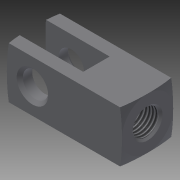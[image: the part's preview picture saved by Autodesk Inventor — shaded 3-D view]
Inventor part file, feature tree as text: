
AUTODESK INVENTOR PART (.ipt)
format: ipt  version: 2014 (Build 180170000, 170)  size: 210,432 bytes
history: native  units: in
note: dims shown in document units (in); Inventor stores cm internally (conversion verified against a paired STEP export)
features: other x126, sketch x7, revolve x3, extrude x2, hole x2
ambient origin geometry x8: Origin, YZ Plane, XZ Plane, XY Plane, X Axis, Y Axis, Z Axis, Center Point
bodies: Solid1 (feature_tree)
feature tree (140):
  extrude  "Extrusion1"  Depth=0.75in TaperAngle=0.0deg
  extrude  "Extrusion2"  TaperAngle=360.0deg  [1 undecoded]
  hole  "Hole1"  [1 undecoded]
  hole  "Hole2"  [1 undecoded]
  revolve  "Revolution1"  [1 undecoded]
  revolve  "Revolution2"  [1 undecoded]
  revolve  "Revolution3"  [1 undecoded]
  other  "dummy_XY"
  other  "dummy_YZ"
  other  "dummy_ZX"
  other  "dummy_X"
  other  "dummy_Y"
  other  "dummy_Z"
  other  "dummy_Center"
  other  "h1_XY"
  other  "h1_YZ"
  other  "h1_ZX"
  other  "h1_X"
  other  "h1_Y"
  other  "h1_Z"
  other  "h1_Center"
  other  "h2_XY"
  other  "h2_YZ"
  other  "h2_ZX"
  other  "h2_X"
  other  "h2_Y"
  other  "h2_Z"
  other  "h2_Center"
  other  "l1_XY"
  other  "l1_YZ"
  other  "l1_ZX"
  other  "l1_X"
  other  "l1_Y"
  other  "l1_Z"
  other  "l1_Center"
  other  "l11_XY"
  other  "l11_YZ"
  other  "l11_ZX"
  other  "l11_X"
  other  "l11_Y"
  other  "l11_Z"
  other  "l11_Center"
  other  "l12_XY"
  other  "l12_YZ"
  other  "l12_ZX"
  other  "l12_X"
  other  "l12_Y"
  other  "l12_Z"
  other  "l12_Center"
  other  "l2_XY"
  other  "l2_YZ"
  other  "l2_ZX"
  other  "l2_X"
  other  "l2_Y"
  other  "l2_Z"
  other  "l2_Center"
  other  "l21_XY"
  other  "l21_YZ"
  other  "l21_ZX"
  other  "l21_X"
  other  "l21_Y"
  other  "l21_Z"
  other  "l21_Center"
  other  "l22_XY"
  other  "l22_YZ"
  other  "l22_ZX"
  other  "l22_X"
  other  "l22_Y"
  other  "l22_Z"
  other  "l22_Center"
  other  "piston_rod_clevis_XY"
  other  "piston_rod_clevis_YZ"
  other  "piston_rod_clevis_ZX"
  other  "piston_rod_clevis_X"
  other  "piston_rod_clevis_Y"
  other  "piston_rod_clevis_Z"
  other  "piston_rod_clevis_Center"
  other  "rod_clevis_body_XY"
  other  "rod_clevis_body_YZ"
  other  "rod_clevis_body_ZX"
  other  "rod_clevis_body_X"
  other  "rod_clevis_body_Y"
  other  "rod_clevis_body_Z"
  other  "rod_clevis_body_Center"
  other  "th1_XY"
  other  "th1_YZ"
  other  "th1_ZX"
  other  "th1_X"
  other  "th1_Y"
  other  "th1_Z"
  other  "th1_Center"
  other  "th2_XY"
  other  "th2_YZ"
  other  "th2_ZX"
  other  "th2_X"
  other  "th2_Y"
  other  "th2_Z"
  other  "th2_Center"
  other  "to_cylinder_XY"
  other  "to_cylinder_YZ"
  other  "to_cylinder_ZX"
  other  "to_cylinder_X"
  other  "to_cylinder_Y"
  other  "to_cylinder_Z"
  other  "to_cylinder_Center"
  other  "w1_XY"
  other  "w1_YZ"
  other  "w1_ZX"
  other  "w1_X"
  other  "w1_Y"
  other  "w1_Z"
  other  "w1_Center"
  other  "w11_XY"
  other  "w11_YZ"
  other  "w11_ZX"
  other  "w11_X"
  other  "w11_Y"
  other  "w11_Z"
  other  "w11_Center"
  other  "w12_XY"
  other  "w12_YZ"
  other  "w12_ZX"
  other  "w12_X"
  other  "w12_Y"
  other  "w12_Z"
  other  "w12_Center"
  other  "w2_XY"
  other  "w2_YZ"
  other  "w2_ZX"
  other  "w2_X"
  other  "w2_Y"
  other  "w2_Z"
  other  "w2_Center"
  sketch  "Sketch_1"  dims[d0=0.75in d1=0.0in d2=0.75in d3=0.0in]
  sketch  "Sketch_2"  dims[d4=0.383in d5=0.62in d6=0.4375in d7=0.25in d8=90.0deg d9=0.62in d10=0.0in]
  sketch  "Sketch3"  dims[d11=0.3906in d12=0.75in d13=0.375in d14=0.25in d15=0.5635in d16=0.13in d17=0.0in d18=360.0deg]
  sketch  "Sketch4"  dims[d19=360.0deg d20=360.0deg]
  sketch  "Sketch_5"
  sketch  "Sketch_9"
  sketch  "Sketch_10"
note: 6 required parameter values undecoded (feature->parameter linkage not recoverable at this tier; creation-order binding heuristic only, values carry confidence <= 0.55)
